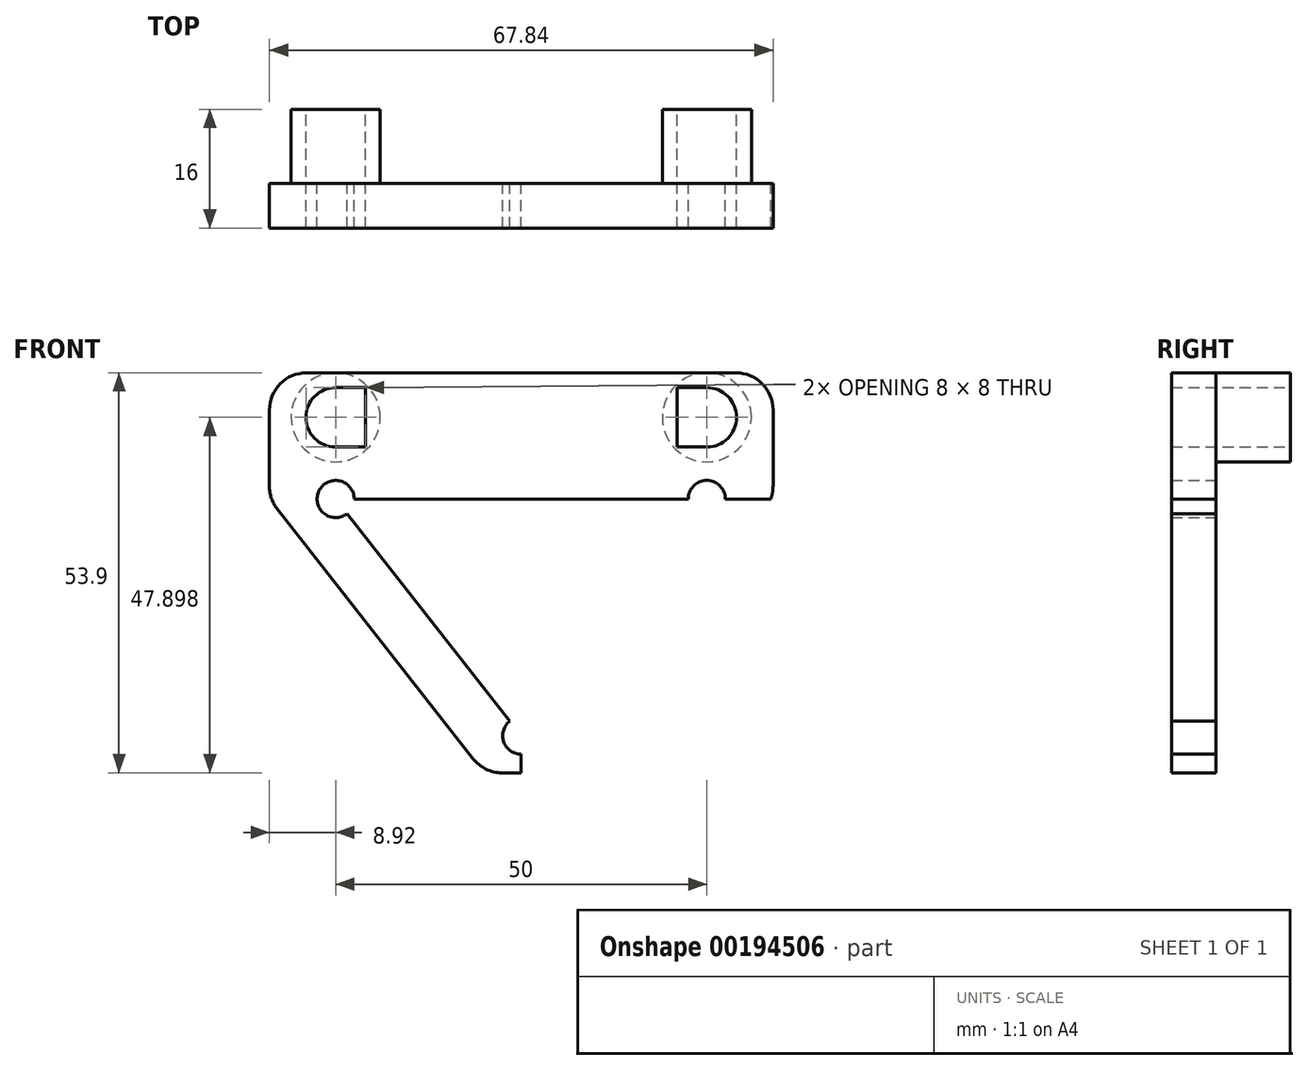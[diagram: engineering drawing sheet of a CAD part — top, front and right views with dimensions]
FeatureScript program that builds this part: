
annotation { "Feature Type Name" : "Feature", "Feature Type Description" : "" }
export const myFeature = defineFeature(function(context is Context, id is Id, definition is map)
    precondition{}
    {
        {
            var Q0;
            Q0=qCreatedBy(makeId("Front.planeOp"),FACE);
            var sketch = newSketch(context, id + "F0", { "sketchPlane" : qUnion([Q0])});
            skPoint(sketch, "E0.middle", {"position": v(0, 0) * mm});
            skPoint(sketch, "E1", {"position": v(0, -17.36) * mm});
            skLineSegment(sketch, "E2", {"start": v(-15.95, 14.54) * mm, "end": v(15.95, 14.54) * mm});
            skLineSegment(sketch, "E3", {"start": v(25, 14.54) * mm, "end": v(15.95, 14.54) * mm});
            skLineSegment(sketch, "E4", {"start": v(-15.95, 14.54) * mm, "end": v(-40.87, 14.54) * mm});
            skLineSegment(sketch, "E5", {"start": v(-76.54, 14.54) * mm, "end": v(86.17, 14.54) * mm});
            skPoint(sketch, "E6", {"position": v(0, 14.54) * mm});
            skPoint(sketch, "E7", {"position": v(25, 14.54) * mm});
            skPoint(sketch, "E8.MirrorP", {"position": v(-25, 14.54) * mm});
            skCircle(sketch, "E9", {"center": v(0, -17.36) * mm, "radius": 2.5 * mm});
            skCircle(sketch, "E10", {"center": v(25, 14.54) * mm, "radius": 2.5 * mm});
            skCircle(sketch, "E11", {"center": v(-25, 14.54) * mm, "radius": 2.5 * mm});
            skLineSegment(sketch, "E12", {"start": v(0, -17.36) * mm, "end": v(0, -22.36) * mm});
            skLineSegment(sketch, "E13", {"start": v(0, -22.36) * mm, "end": v(5, -22.36) * mm});
            skLineSegment(sketch, "E14", {"start": v(2.57, -22.36) * mm, "end": v(0, -22.36) * mm});
            skLineSegment(sketch, "E15", {"start": v(0, -22.36) * mm, "end": v(-2.57, -22.36) * mm});
            skLineSegment(sketch, "E16", {"start": v(-25, 14.54) * mm, "end": v(0, -17.36) * mm});
            skLineSegment(sketch, "E17", {"start": v(0, -17.36) * mm, "end": v(25, 14.54) * mm});
            skLineSegment(sketch, "E18", {"start": v(-25, 14.54) * mm, "end": v(25, 14.54) * mm});
            skLineSegment(sketch, "E19", {"start": v(6.5, -20.45) * mm, "end": v(32.85, 13.18) * mm});
            skLineSegment(sketch, "E20", {"start": v(-6.5, -20.45) * mm, "end": v(-32.85, 13.18) * mm});
            skLineSegment(sketch, "E21", {"start": v(-33.92, 16.26) * mm, "end": v(-33.92, 19.54) * mm});
            skLineSegment(sketch, "E22", {"start": v(-33.92, 19.54) * mm, "end": v(33.92, 19.54) * mm});
            skLineSegment(sketch, "E23", {"start": v(33.92, 19.54) * mm, "end": v(33.92, 16.26) * mm});
            skLineSegment(sketch, "E24", {"start": v(33.92, 19.54) * mm, "end": v(33.92, 26.54) * mm});
            skLineSegment(sketch, "E25", {"start": v(-33.92, 19.54) * mm, "end": v(-33.92, 26.54) * mm});
            skLineSegment(sketch, "E26", {"start": v(-28.92, 31.54) * mm, "end": v(28.92, 31.54) * mm});
            skPoint(sketch, "E27.visualSharp", {"position": v(-33.92, 31.54) * mm});
            skArc(sketch, "E27.filletArc", {"start": v(-28.92, 31.54) * mm, "mid": v(-32.45, 30.07) * mm, "end": v(-33.92, 26.54) * mm});
            skPoint(sketch, "E28.visualSharp", {"position": v(33.92, 31.54) * mm});
            skArc(sketch, "E28.filletArc", {"start": v(33.92, 26.54) * mm, "mid": v(32.45, 30.07) * mm, "end": v(28.92, 31.54) * mm});
            skPoint(sketch, "E29.visualSharp", {"position": v(33.92, 14.54) * mm});
            skArc(sketch, "E29.filletArc", {"start": v(32.85, 13.18) * mm, "mid": v(33.64, 14.63) * mm, "end": v(33.92, 16.26) * mm});
            skPoint(sketch, "E30.visualSharp", {"position": v(5, -22.36) * mm});
            skArc(sketch, "E30.filletArc", {"start": v(2.57, -22.36) * mm, "mid": v(4.75, -21.86) * mm, "end": v(6.5, -20.45) * mm});
            skPoint(sketch, "E31.visualSharp", {"position": v(-5, -22.36) * mm});
            skArc(sketch, "E31.filletArc", {"start": v(-6.5, -20.45) * mm, "mid": v(-4.75, -21.86) * mm, "end": v(-2.57, -22.36) * mm});
            skPoint(sketch, "E32.visualSharp", {"position": v(-33.92, 14.54) * mm});
            skArc(sketch, "E32.filletArc", {"start": v(-33.92, 16.26) * mm, "mid": v(-33.64, 14.63) * mm, "end": v(-32.85, 13.18) * mm});
            skLineSegment(sketch, "E33", {"start": v(-25, 19.54) * mm, "end": v(-25, 31.54) * mm});
            skLineSegment(sketch, "E34", {"start": v(25, 19.54) * mm, "end": v(25, 31.54) * mm});
            skPoint(sketch, "E35", {"position": v(-25, 25.54) * mm});
            skPoint(sketch, "E36", {"position": v(25, 25.54) * mm});
            skCircle(sketch, "E37", {"center": v(-25, 25.54) * mm, "radius": 4 * mm});
            skCircle(sketch, "E38", {"center": v(25, 25.54) * mm, "radius": 4 * mm});
            skLineSegment(sketch, "E39", {"start": v(25, 21.54) * mm, "end": v(21, 21.54) * mm});
            skLineSegment(sketch, "E40", {"start": v(21, 21.54) * mm, "end": v(21, 25.54) * mm});
            skLineSegment(sketch, "E41", {"start": v(21, 25.54) * mm, "end": v(21, 29.54) * mm});
            skLineSegment(sketch, "E42", {"start": v(21, 29.54) * mm, "end": v(25, 29.54) * mm});
            skLineSegment(sketch, "E43.MirrorCS", {"start": v(-25, 29.54) * mm, "end": v(-21, 29.54) * mm});
            skLineSegment(sketch, "E44.MirrorCS", {"start": v(-21, 21.54) * mm, "end": v(-21, 29.54) * mm});
            skLineSegment(sketch, "E45.MirrorCS", {"start": v(-25, 21.54) * mm, "end": v(-21, 21.54) * mm});
            skSolve(sketch);
        }
        {
            var Q0;
            {var subQ7=sQuery(id+"F0.wireOp",EDGE,"E25");Q0=makeQuery(id+"F0.imprint","IMPRINT",FACE,{"disambiguationData":[TD([[makeQuery(id+"F0.imprint","IMPRINT",EDGE,{"derivedFrom":subQ7}),-1.0]])]});}
            var Q1;
            {var subQ0=sQuery(id+"F0.wireOp",EDGE,"E33");var subQ5=sQuery(id+"F0.wireOp",EDGE,"E22");var subQ6=makeQuery(id+"F0.imprint","INTERSECT",VERTEX,{"derivedFrom":[subQ5,subQ0]});Q1=makeQuery(id+"F0.imprint","IMPRINT",FACE,{"disambiguationData":[TD([[makeQuery(id+"F0.imprint","IMPRINT",EDGE,{"disambiguationData":[TD([[subQ6,-1.0]])],"derivedFrom":subQ5}),1.0]])]});}
            var Q2;
            {var subQ1=sQuery(id+"F0.wireOp",EDGE,"E24");Q2=makeQuery(id+"F0.imprint","IMPRINT",FACE,{"disambiguationData":[TD([[makeQuery(id+"F0.imprint","IMPRINT",EDGE,{"derivedFrom":subQ1}),1.0]])]});}
            var Q3;
            {var subQ8=sQuery(id+"F0.wireOp",EDGE,"E21");Q3=makeQuery(id+"F0.imprint","IMPRINT",FACE,{"disambiguationData":[TD([[makeQuery(id+"F0.imprint","IMPRINT",EDGE,{"derivedFrom":subQ8}),-1.0]])]});}
            var Q4;
            {var subQ5=sQuery(id+"F0.wireOp",EDGE,"E18");var subQ6=makeQuery(id+"F0.imprint","IMPRINT",VERTEX,{"disambiguationData":[OD(0.0)],"derivedFrom":subQ5});Q4=makeQuery(id+"F0.imprint","IMPRINT",FACE,{"disambiguationData":[TD([[makeQuery(id+"F0.imprint","IMPRINT",EDGE,{"disambiguationData":[TD([[subQ6,-1.0]])],"derivedFrom":subQ5}),-1.0]])]});}
            var Q5;
            {var subQ0=sQuery(id+"F0.wireOp",EDGE,"E14");Q5=makeQuery(id+"F0.imprint","IMPRINT",FACE,{"disambiguationData":[TD([[makeQuery(id+"F0.imprint","IMPRINT",EDGE,{"derivedFrom":subQ0}),-1.0]])]});}
            var Q6;
            {var subQ0=sQuery(id+"F0.wireOp",EDGE,"E15");Q6=makeQuery(id+"F0.imprint","IMPRINT",FACE,{"disambiguationData":[TD([[makeQuery(id+"F0.imprint","IMPRINT",EDGE,{"derivedFrom":subQ0}),-1.0]])]});}
            extrude(context, id + "F1", {"entities" : qUnion([Q0, Q1, Q2, Q3, Q4, Q5, Q6]), "depth" : 6 * mm});
        }
        {
            var Q0;
            Q0=makeQuery(id+"F1.opExtrude","CAP_FACE",FACE,{"disambiguationData":[OSD([sQuery(id+"F0.wireOp",EDGE,"E9"),sQuery(id+"F0.wireOp",EDGE,"E10"),sQuery(id+"F0.wireOp",EDGE,"E11"),sQuery(id+"F0.wireOp",EDGE,"E14"),sQuery(id+"F0.wireOp",EDGE,"E15"),sQuery(id+"F0.wireOp",EDGE,"E19"),sQuery(id+"F0.wireOp",EDGE,"E20"),sQuery(id+"F0.wireOp",EDGE,"E21"),sQuery(id+"F0.wireOp",EDGE,"E23"),sQuery(id+"F0.wireOp",EDGE,"E24"),sQuery(id+"F0.wireOp",EDGE,"E25"),sQuery(id+"F0.wireOp",EDGE,"E26"),sQuery(id+"F0.wireOp",EDGE,"E27.filletArc"),sQuery(id+"F0.wireOp",EDGE,"E28.filletArc"),sQuery(id+"F0.wireOp",EDGE,"E29.filletArc"),sQuery(id+"F0.wireOp",EDGE,"E30.filletArc"),sQuery(id+"F0.wireOp",EDGE,"E31.filletArc"),sQuery(id+"F0.wireOp",EDGE,"E32.filletArc"),sQuery(id+"F0.wireOp",EDGE,"E37"),sQuery(id+"F0.wireOp",EDGE,"E38")])],"isStart":true});
            var sketch = newSketch(context, id + "F2", { "sketchPlane" : qUnion([Q0])});
            skCircle(sketch, "E46", {"center": v(-25, 25.54) * mm, "radius": 6 * mm});
            skCircle(sketch, "E47", {"center": v(25, 25.54) * mm, "radius": 6 * mm});
            skLineSegment(sketch, "E48", {"start": v(-21, 21.54) * mm, "end": v(-21, 29.54) * mm});
            skLineSegment(sketch, "E49", {"start": v(-21, 29.54) * mm, "end": v(-25, 29.54) * mm});
            skLineSegment(sketch, "E50", {"start": v(-25, 21.54) * mm, "end": v(-21, 21.54) * mm});
            skArc(sketch, "E51", {"start": v(-25, 29.54) * mm, "mid": v(-29, 25.54) * mm, "end": v(-25, 21.54) * mm});
            skLineSegment(sketch, "E52", {"start": v(25, 29.54) * mm, "end": v(21, 29.54) * mm});
            skLineSegment(sketch, "E53", {"start": v(21, 29.54) * mm, "end": v(21, 21.54) * mm});
            skLineSegment(sketch, "E54", {"start": v(21, 21.54) * mm, "end": v(25, 21.54) * mm});
            skArc(sketch, "E55", {"start": v(25, 21.54) * mm, "mid": v(29, 25.54) * mm, "end": v(25, 29.54) * mm});
            skSolve(sketch);
        }
        {
            var Q0;
            Q0=makeQuery(id+"F2.imprint","IMPRINT",FACE,{"disambiguationData":[TD([[makeQuery(id+"F2.imprint","IMPRINT",EDGE,{"derivedFrom":sQuery(id+"F2.wireOp",EDGE,"E46")}),1.0]])]});
            var Q1;
            Q1=makeQuery(id+"F2.imprint","IMPRINT",FACE,{"disambiguationData":[TD([[makeQuery(id+"F2.imprint","IMPRINT",EDGE,{"derivedFrom":sQuery(id+"F2.wireOp",EDGE,"E47")}),1.0]])]});
            extrude(context, id + "F3", {"entities" : qUnion([Q0, Q1]), "operationType" : NewBodyOperationType.ADD, "depth" : 10 * mm});
        }
    });
